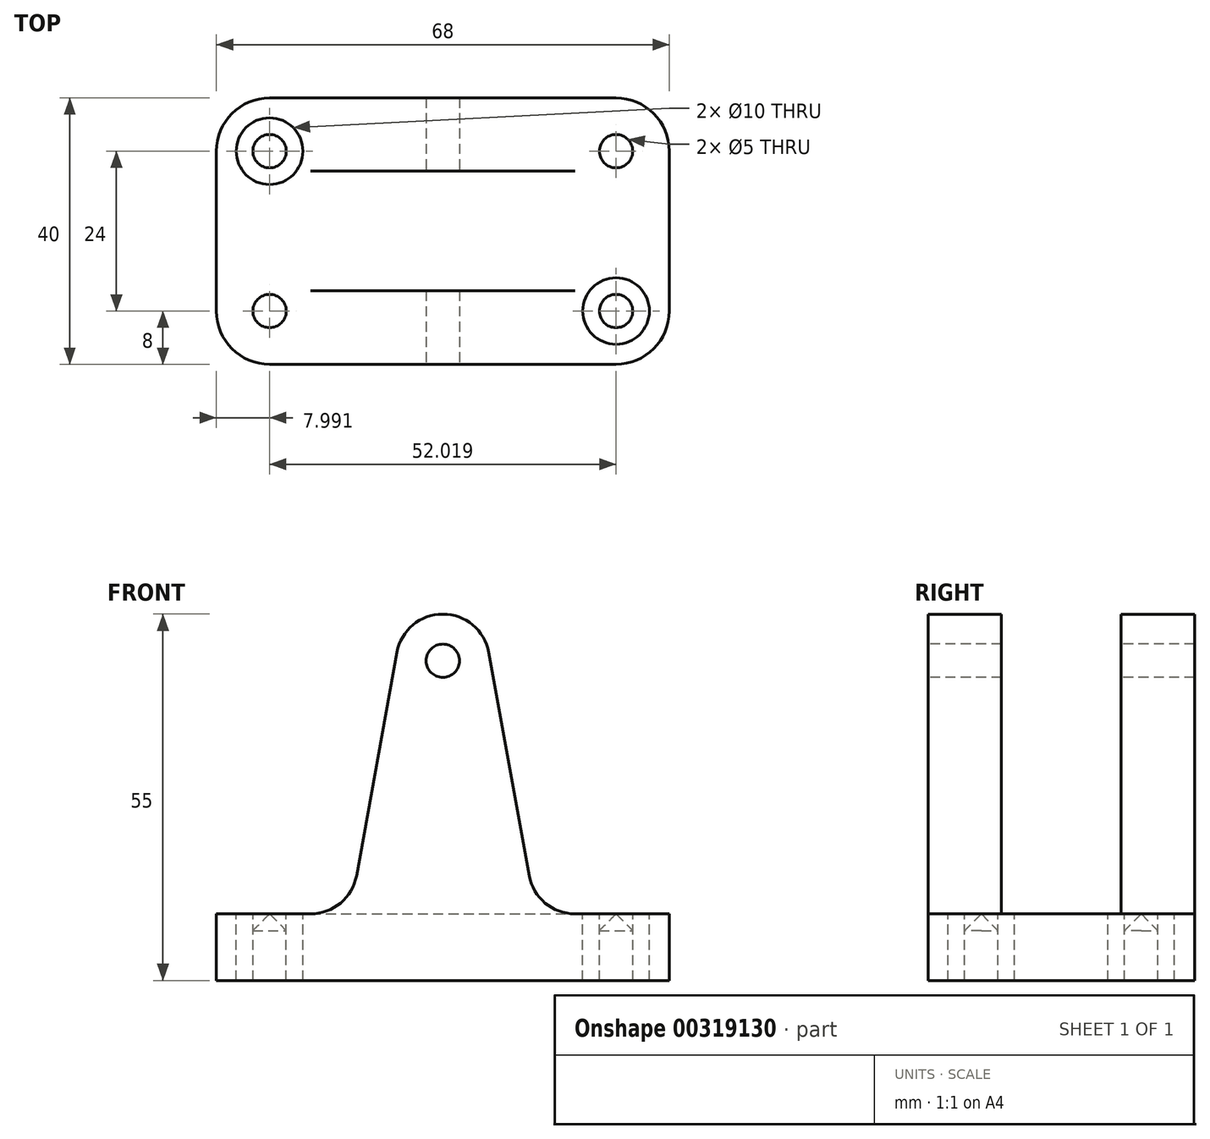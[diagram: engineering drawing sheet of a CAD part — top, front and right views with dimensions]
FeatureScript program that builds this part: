
annotation { "Feature Type Name" : "Feature", "Feature Type Description" : "" }
export const myFeature = defineFeature(function(context is Context, id is Id, definition is map)
    precondition{}
    {
        {
            var Q0;
            Q0=qCreatedBy(makeId("Front.planeOp"),FACE);
            var sketch = newSketch(context, id + "F0", { "sketchPlane" : qUnion([Q0])});
            skLineSegment(sketch, "E0", {"start": v(0, -39.8) * mm, "end": v(-34, -39.8) * mm});
            skLineSegment(sketch, "E1", {"start": v(0, -39.8) * mm, "end": v(34, -39.8) * mm});
            skLineSegment(sketch, "E2", {"start": v(34, -39.8) * mm, "end": v(34, -29.8) * mm});
            skLineSegment(sketch, "E3.MirrorCS", {"start": v(-34, -39.8) * mm, "end": v(-34, -29.8) * mm});
            skLineSegment(sketch, "E4", {"start": v(-34, -29.8) * mm, "end": v(34, -29.8) * mm});
            skLineSegment(sketch, "E5", {"start": v(0, -39.8) * mm, "end": v(0, 8.2) * mm, "construction": true});
            skCircle(sketch, "E6", {"center": v(0, 8.2) * mm, "radius": 2.5 * mm});
            skArc(sketch, "E7", {"start": v(6.89, 9.45) * mm, "mid": v(0, 15.2) * mm, "end": v(-6.89, 9.45) * mm});
            skLineSegment(sketch, "E8", {"start": v(14, -29.8) * mm, "end": v(6.89, 9.45) * mm});
            skLineSegment(sketch, "E9", {"start": v(-14, -29.8) * mm, "end": v(-6.89, 9.45) * mm});
            skSolve(sketch);
        }
        {
            var Q0;
            Q0=makeQuery(id+"F0.imprint","IMPRINT",FACE,{"disambiguationData":[TD([[makeQuery(id+"F0.imprint","IMPRINT",EDGE,{"derivedFrom":sQuery(id+"F0.wireOp",EDGE,"E6")}),-1.0]])]});
            var Q1;
            Q1=makeQuery(id+"F0.imprint","IMPRINT",FACE,{"disambiguationData":[TD([[makeQuery(id+"F0.imprint","IMPRINT",EDGE,{"derivedFrom":sQuery(id+"F0.wireOp",EDGE,"E0")}),-1.0]])]});
            extrude(context, id + "F1", {"entities" : qUnion([Q0, Q1]), "oppositeDirection" : true, "depth" : 40 * mm});
        }
        {
            var Q0;
            {var subQ0=sQuery(id+"F0.wireOp",EDGE,"E4");Q0=makeQuery(id+"F1.opExtrude","SWEPT_FACE",FACE,{"disambiguationData":[OSD([subQ0]),TDD([makeQuery(id+"F0.imprint","IMPRINT",EDGE,{"disambiguationData":[TD([[makeQuery(id+"F0.imprint","INTERSECT",VERTEX,{"derivedFrom":[sQuery(id+"F0.wireOp",EDGE,"E3.MirrorCS"),subQ0]}),-1.0]])],"derivedFrom":subQ0})])]});}
            var sketch = newSketch(context, id + "F2", { "sketchPlane" : qUnion([Q0])});
            skCircle(sketch, "E10.MirrorC", {"center": v(26, 32) * mm, "radius": 2.5 * mm});
            skCircle(sketch, "E11.MirrorC", {"center": v(26, 32) * mm, "radius": 5 * mm});
            skCircle(sketch, "E12.MirrorC", {"center": v(-26, 32) * mm, "radius": 2.5 * mm});
            skCircle(sketch, "E13.MirrorC", {"center": v(-26, 32) * mm, "radius": 5 * mm});
            skCircle(sketch, "E14.MirrorC", {"center": v(-26, 8) * mm, "radius": 2.5 * mm});
            skCircle(sketch, "E15.MirrorC", {"center": v(-26, 8) * mm, "radius": 5 * mm});
            skCircle(sketch, "E16.MirrorC", {"center": v(26, 8) * mm, "radius": 2.5 * mm});
            skCircle(sketch, "E17.MirrorC", {"center": v(26, 8) * mm, "radius": 5 * mm});
            skLineSegment(sketch, "E18", {"start": v(-26, 37) * mm, "end": v(-26, 27) * mm, "construction": true});
            skLineSegment(sketch, "E19", {"start": v(-26, 13) * mm, "end": v(-26, 3) * mm, "construction": true});
            skLineSegment(sketch, "E20", {"start": v(26, 37) * mm, "end": v(26, 27) * mm, "construction": true});
            skLineSegment(sketch, "E21", {"start": v(26, 13) * mm, "end": v(26, 3) * mm, "construction": true});
            skLineSegment(sketch, "E22", {"start": v(31, 8) * mm, "end": v(21, 8) * mm, "construction": true});
            skLineSegment(sketch, "E23", {"start": v(31, 32) * mm, "end": v(21, 32) * mm, "construction": true});
            skLineSegment(sketch, "E24", {"start": v(-31, 8) * mm, "end": v(-21, 8) * mm, "construction": true});
            skLineSegment(sketch, "E25", {"start": v(-31, 32) * mm, "end": v(-21, 32) * mm, "construction": true});
            skSolve(sketch);
        }
        {
            var Q0;
            Q0 = qSketchRegion(id + "F2", true);
            extrude(context, id + "F3", {"entities" : qUnion([Q0]), "operationType" : NewBodyOperationType.REMOVE, "oppositeDirection" : true, "depth" : 3 * mm});
        }
        {
            var Q0;
            {var subQ1=sQuery(id+"F0.wireOp",EDGE,"E3.MirrorCS");var subQ5=sQuery(id+"F0.wireOp",EDGE,"E4");Q0=makeQuery(id+"F3.boolean.opBoolean","SPLIT",FACE,{"disambiguationData":[TD([makeQuery(id+"F1.opExtrude","SWEPT_FACE",FACE,{"disambiguationData":[OSD([subQ1])]})])],"derivedFrom":makeQuery(id+"F1.opExtrude","SWEPT_FACE",FACE,{"disambiguationData":[OSD([subQ5]),TDD([makeQuery(id+"F0.imprint","IMPRINT",EDGE,{"disambiguationData":[TD([[makeQuery(id+"F0.imprint","INTERSECT",VERTEX,{"derivedFrom":[subQ1,subQ5]}),-1.0]])],"derivedFrom":subQ5})])]})});}
            var sketch = newSketch(context, id + "F4", { "sketchPlane" : qUnion([Q0])});
            skLineSegment(sketch, "E26", {"start": v(-34, 0) * mm, "end": v(-34, 20) * mm, "construction": true});
            skLineSegment(sketch, "E27", {"start": v(-34, 20) * mm, "end": v(0, 20) * mm, "construction": true});
            skLineSegment(sketch, "E28", {"start": v(0, 20) * mm, "end": v(0, 32) * mm, "construction": true});
            skLineSegment(sketch, "E29", {"start": v(0, 20) * mm, "end": v(0, 8) * mm, "construction": true});
            skLineSegment(sketch, "E30", {"start": v(-18.64, 28.99) * mm, "end": v(18.64, 28.99) * mm});
            skLineSegment(sketch, "E31.MirrorCS", {"start": v(-18.64, 11.01) * mm, "end": v(18.64, 11.01) * mm});
            skLineSegment(sketch, "E32", {"start": v(18.64, 28.99) * mm, "end": v(18.64, 11.01) * mm});
            skLineSegment(sketch, "E33.MirrorCS", {"start": v(-18.64, 28.99) * mm, "end": v(-18.64, 11.01) * mm});
            skPoint(sketch, "E34.orphan", {"position": v(30, 28.99) * mm});
            skPoint(sketch, "E35.orphan", {"position": v(30, 11.01) * mm});
            skPoint(sketch, "E36.orphan", {"position": v(-30, 28.99) * mm});
            skPoint(sketch, "E37.orphan", {"position": v(-30, 11.01) * mm});
            skSolve(sketch);
        }
        {
            var Q0;
            {var subQ0=sQuery(id+"F4.wireOp",EDGE,"f66d0ab9-449e-4d87-a520-3055bb65471c0.MirrorCS");var subQ1=sQuery(id+"F4.wireOp",EDGE,"E30");var subQ2=makeQuery(id+"F4.imprint","INTERSECT",VERTEX,{"derivedFrom":[subQ1,subQ0]});Q0=makeQuery(id+"F4.imprint","IMPRINT",FACE,{"disambiguationData":[TD([[makeQuery(id+"F4.imprint","IMPRINT",EDGE,{"disambiguationData":[TD([[subQ2,1.0]])],"derivedFrom":subQ0}),1.0]])]});}
            var Q1;
            {var subQ0=sQuery(id+"F4.wireOp",EDGE,"E30");var subQ6=makeQuery(id+"F3.boolean.opBoolean","COPY",EDGE,{"derivedFrom":makeQuery(id+"F3.opExtrude","CAP_EDGE",EDGE,{"disambiguationData":[OSD([sQuery(id+"F2.wireOp",EDGE,"E13.MirrorC")])],"isStart":true})});var subQ11=makeQuery(id+"F4.imprint","INTERSECT",VERTEX,{"derivedFrom":[subQ6,subQ0]});Q1=makeQuery(id+"F4.imprint","IMPRINT",FACE,{"disambiguationData":[TD([[makeQuery(id+"F4.imprint","IMPRINT",EDGE,{"disambiguationData":[TD([[subQ11,-1.0]])],"derivedFrom":subQ0}),-1.0]])]});}
            extrude(context, id + "F5", {"entities" : qUnion([Q0, Q1]), "operationType" : NewBodyOperationType.REMOVE, "depth" : 50 * mm});
        }
        {
            var Q0;
            Q0=makeQuery(id+"F1.opExtrude","CAP_EDGE",EDGE,{"disambiguationData":[OSD([sQuery(id+"F0.wireOp",EDGE,"E3.MirrorCS")])],"isStart":true});
            var Q1;
            Q1=makeQuery(id+"F1.opExtrude","CAP_EDGE",EDGE,{"disambiguationData":[OSD([sQuery(id+"F0.wireOp",EDGE,"E2")])],"isStart":true});
            var Q2;
            Q2=makeQuery(id+"F1.opExtrude","CAP_EDGE",EDGE,{"disambiguationData":[OSD([sQuery(id+"F0.wireOp",EDGE,"E2")])],"isStart":false});
            var Q3;
            Q3=makeQuery(id+"F1.opExtrude","CAP_EDGE",EDGE,{"disambiguationData":[OSD([sQuery(id+"F0.wireOp",EDGE,"E3.MirrorCS")])],"isStart":false});
            fillet(context, id + "F6", {"entities" : qUnion([Q0, Q1, Q2, Q3]), "radius" : 8 * mm, "tangentPropagation" : true, "allowEdgeOverflow" : false});
        }
        {
            var Q0;
            Q0=makeQuery(id+"F3.boolean.opBoolean","COPY",FACE,{"derivedFrom":makeQuery(id+"F3.opExtrude","CAP_FACE",FACE,{"disambiguationData":[OSD([sQuery(id+"F2.wireOp",EDGE,"E12.MirrorC"),sQuery(id+"F2.wireOp",EDGE,"E13.MirrorC")])],"isStart":false})});
            var sketch = newSketch(context, id + "F7", { "sketchPlane" : qUnion([Q0])});
            skCircle(sketch, "E38", {"center": v(-26, 32) * mm, "radius": 2.5 * mm});
            skCircle(sketch, "E39", {"center": v(-26, 32) * mm, "radius": 5 * mm});
            skCircle(sketch, "E40.MirrorC", {"center": v(26, 32) * mm, "radius": 2.5 * mm});
            skCircle(sketch, "E41.MirrorC", {"center": v(26, 32) * mm, "radius": 5 * mm});
            skCircle(sketch, "E42.MirrorC", {"center": v(26, 8) * mm, "radius": 2.5 * mm});
            skCircle(sketch, "E43.MirrorC", {"center": v(26, 8) * mm, "radius": 5 * mm});
            skCircle(sketch, "E44.MirrorC", {"center": v(-26, 8) * mm, "radius": 2.5 * mm});
            skCircle(sketch, "E45.MirrorC", {"center": v(-26, 8) * mm, "radius": 5 * mm});
            skSolve(sketch);
        }
        {
            var Q0;
            Q0=makeQuery(id+"F0.imprint","IMPRINT",FACE,{"disambiguationData":[TD([[makeQuery(id+"F0.imprint","IMPRINT",EDGE,{"derivedFrom":sQuery(id+"F0.wireOp",EDGE,"E0")}),-1.0]])]});
            cPlane(context, id + "F8", {"entities" : qUnion([Q0]), "cplaneType" : CPlaneType.OFFSET, "offset" : 8 * mm, "oppositeDirection" : true, "width" : 150 * mm, "height" : 150 * mm});
        }
        {
            var Q0;
            {var subQ0=sQuery(id+"F0.wireOp",EDGE,"E9");var subQ1=sQuery(id+"F0.wireOp",EDGE,"E4");var subQ5=sQuery(id+"F4.wireOp",EDGE,"E31.MirrorCS");Q0=makeQuery(id+"F5.boolean.opBoolean","SPLIT",EDGE,{"disambiguationData":[TD([makeQuery(id+"F5.opExtrude","SWEPT_FACE",FACE,{"disambiguationData":[OSD([subQ5])]})])],"derivedFrom":makeQuery(id+"F1.opExtrude","SWEPT_EDGE",EDGE,{"disambiguationData":[OSD([subQ1,subQ0])]})});}
            var Q1;
            {var subQ0=sQuery(id+"F0.wireOp",EDGE,"E4");var subQ3=sQuery(id+"F0.wireOp",EDGE,"E9");var subQ5=sQuery(id+"F4.wireOp",EDGE,"E30");Q1=makeQuery(id+"F5.boolean.opBoolean","SPLIT",EDGE,{"disambiguationData":[TD([makeQuery(id+"F5.opExtrude","SWEPT_FACE",FACE,{"disambiguationData":[OSD([subQ5])]})])],"derivedFrom":makeQuery(id+"F1.opExtrude","SWEPT_EDGE",EDGE,{"disambiguationData":[OSD([subQ0,subQ3])]})});}
            var Q2;
            {var subQ0=sQuery(id+"F0.wireOp",EDGE,"E8");var subQ1=sQuery(id+"F0.wireOp",EDGE,"E4");var subQ5=sQuery(id+"F4.wireOp",EDGE,"E31.MirrorCS");Q2=makeQuery(id+"F5.boolean.opBoolean","SPLIT",EDGE,{"disambiguationData":[TD([makeQuery(id+"F5.opExtrude","SWEPT_FACE",FACE,{"disambiguationData":[OSD([subQ5])]})])],"derivedFrom":makeQuery(id+"F1.opExtrude","SWEPT_EDGE",EDGE,{"disambiguationData":[OSD([subQ1,subQ0])]})});}
            var Q3;
            {var subQ0=sQuery(id+"F0.wireOp",EDGE,"E8");var subQ1=sQuery(id+"F0.wireOp",EDGE,"E4");var subQ5=sQuery(id+"F4.wireOp",EDGE,"E30");Q3=makeQuery(id+"F5.boolean.opBoolean","SPLIT",EDGE,{"disambiguationData":[TD([makeQuery(id+"F5.opExtrude","SWEPT_FACE",FACE,{"disambiguationData":[OSD([subQ5])]})])],"derivedFrom":makeQuery(id+"F1.opExtrude","SWEPT_EDGE",EDGE,{"disambiguationData":[OSD([subQ1,subQ0])]})});}
            fillet(context, id + "F9", {"entities" : qUnion([Q0, Q1, Q2, Q3]), "radius" : 7 * mm, "tangentPropagation" : true, "allowEdgeOverflow" : false});
        }
        {
            var Q0;
            Q0 = qSketchRegion(id + "F7", true);
            extrude(context, id + "F10", {"entities" : qUnion([Q0]), "operationType" : NewBodyOperationType.ADD, "depth" : 3 * mm});
        }
        {
            var Q0;
            Q0=makeQuery(id+"F2.imprint","IMPRINT",FACE,{"disambiguationData":[TD([[makeQuery(id+"F2.imprint","IMPRINT",EDGE,{"derivedFrom":sQuery(id+"F2.wireOp",EDGE,"E12.MirrorC")}),-1.0]])]});
            var Q1;
            Q1=makeQuery(id+"F2.imprint","IMPRINT",FACE,{"disambiguationData":[TD([[makeQuery(id+"F2.imprint","IMPRINT",EDGE,{"derivedFrom":sQuery(id+"F2.wireOp",EDGE,"E14.MirrorC")}),1.0]])]});
            var Q2;
            Q2=makeQuery(id+"F2.imprint","IMPRINT",FACE,{"disambiguationData":[TD([[makeQuery(id+"F2.imprint","IMPRINT",EDGE,{"derivedFrom":sQuery(id+"F2.wireOp",EDGE,"E16.MirrorC")}),-1.0]])]});
            var Q3;
            Q3=makeQuery(id+"F2.imprint","IMPRINT",FACE,{"disambiguationData":[TD([[makeQuery(id+"F2.imprint","IMPRINT",EDGE,{"derivedFrom":sQuery(id+"F2.wireOp",EDGE,"E10.MirrorC")}),1.0]])]});
            extrude(context, id + "F11", {"entities" : qUnion([Q0, Q1, Q2, Q3]), "operationType" : NewBodyOperationType.REMOVE, "oppositeDirection" : true, "depth" : 25 * mm});
        }
        {
            var Q0;
            Q0=makeQuery(id+"F11.boolean.opBoolean","COPY",EDGE,{"derivedFrom":makeQuery(id+"F11.opExtrude","CAP_EDGE",EDGE,{"disambiguationData":[OSD([sQuery(id+"F2.wireOp",EDGE,"E12.MirrorC")])],"isStart":true})});
            var Q1;
            Q1=makeQuery(id+"F11.boolean.opBoolean","COPY",EDGE,{"derivedFrom":makeQuery(id+"F11.opExtrude","CAP_EDGE",EDGE,{"disambiguationData":[OSD([sQuery(id+"F2.wireOp",EDGE,"E10.MirrorC")])],"isStart":true})});
            var Q2;
            Q2=makeQuery(id+"F11.boolean.opBoolean","COPY",EDGE,{"derivedFrom":makeQuery(id+"F11.opExtrude","CAP_EDGE",EDGE,{"disambiguationData":[OSD([sQuery(id+"F2.wireOp",EDGE,"E16.MirrorC")])],"isStart":true})});
            var Q3;
            Q3=makeQuery(id+"F11.boolean.opBoolean","COPY",EDGE,{"derivedFrom":makeQuery(id+"F11.opExtrude","CAP_EDGE",EDGE,{"disambiguationData":[OSD([sQuery(id+"F2.wireOp",EDGE,"E14.MirrorC")])],"isStart":true})});
            chamfer(context, id + "F12", {"entities" : qUnion([Q0, Q1, Q2, Q3]), "chamferType" : ChamferType.OFFSET_ANGLE, "width" : 2.5 * mm, "oppositeDirection" : false, "angle" : 45 * degree, "tangentPropagation" : true});
        }
    });
